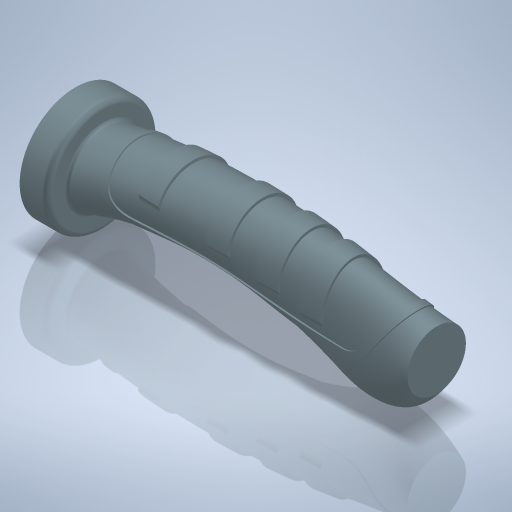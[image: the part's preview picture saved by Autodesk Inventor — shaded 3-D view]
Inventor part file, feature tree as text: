
AUTODESK INVENTOR PART (.ipt)
format: ipt  version: 2024 (Build 280153000, 153)  size: 2,110,976 bytes
history: native  units: mm
features: other x15, sketch x6, plane x4, fillet x3, loft x1, shell x1, extrude x1, projected_geometry x1
ambient origin geometry x8: Origin, YZ Plane, XZ Plane, XY Plane, X Axis, Y Axis, Z Axis, Center Point
bodies: Body1 (feature_tree)
feature tree (32):
  sketch  "Skizze6"  dims[d35=240.0mm d36=550.0mm d37=210.0mm]
  plane  "Arbeitsebene3"
  sketch  "Skizze7"  dims[d38=40.0mm d39=42.0mm d40=52.0mm d41=0.0mm d42=52.0mm]
  plane  "Arbeitsebene4"
  loft  "Erhebung1"
  shell  "Wandung1"  Thickness=210.0mm
  extrude  "Extrusion4"  Depth=42.0mm
  fillet  "Rundung2"  Radius=52.0mm
  fillet  "Rundung3"  [1 undecoded]
  plane  "Arbeitsebene7"
  sketch  "Skizze10"  dims[d44=42.0mm]
  other  "3D-Skizze4"
  other  "Trennen1"
  other  "Trennen2"
  other  "Trennen3"
  other  "Trennen4"
  other  "Verdickung1"
  other  "Verdickung2"
  other  "Verdickung3"
  other  "Verdickung4"
  plane  "Arbeitsebene8"
  sketch  "Skizze15"  dims[d47=0.0mm d48=90.0deg d49=0.0mm d50=90.0deg d51=0.0mm d52=90.0deg d53=2.0mm d57=26.0mm d59=2.0mm d60=15.0mm d61=15.0mm d62=15.0mm d63=15.0mm d64=60.0mm d65=90.0mm d66=125.0mm d69=80.0mm d70=20.0mm d71=0.0mm d72=4.0mm d73=2.0mm d74=20.0mm d75=5.0mm d76=5.0mm d77=5.0mm d78=70.0mm d79=2.0mm d80=2.0mm d81=2.0mm d82=2.0mm d83=2.0mm d84=2.0mm d85=2.0mm d86=2.0mm d87=2.0mm d88=2.0mm d89=2.0mm d90=2.0mm d91=26.0mm d92=2.0mm d96=2.0mm d97=5.0mm d99=20.0mm d100=12.0mm d102=2.0mm d103=2.0mm d107=45.0mm d110=12.0mm d120=22.0mm d121=20.0mm d124=150.0mm d125=65.0mm d126=1.0mm d127=1.0mm d128=5.0mm d14=0.5mm d15=0.872665mm d16=0.5mm d17=0.872665mm]
  other  "3D-Skizze6"
  other  "Trennen5"
  other  "Trennen6"
  other  "Verdickung5"
  fillet  "Rundung4"  Radius=52.0mm
  sketch  "Skizze8"  dims[d43=240.0mm]
  projected_geometry  "Projizierte Kontur2"
  sketch  "Skizze11"  dims[d45=0.0mm d46=90.0deg]
  other  "Projekt aus Skizze10"
  other  "Auf Fläche projizieren2"
note: 1 required parameter value undecoded (feature->parameter linkage not recoverable at this tier; creation-order binding heuristic only, values carry confidence <= 0.55)
